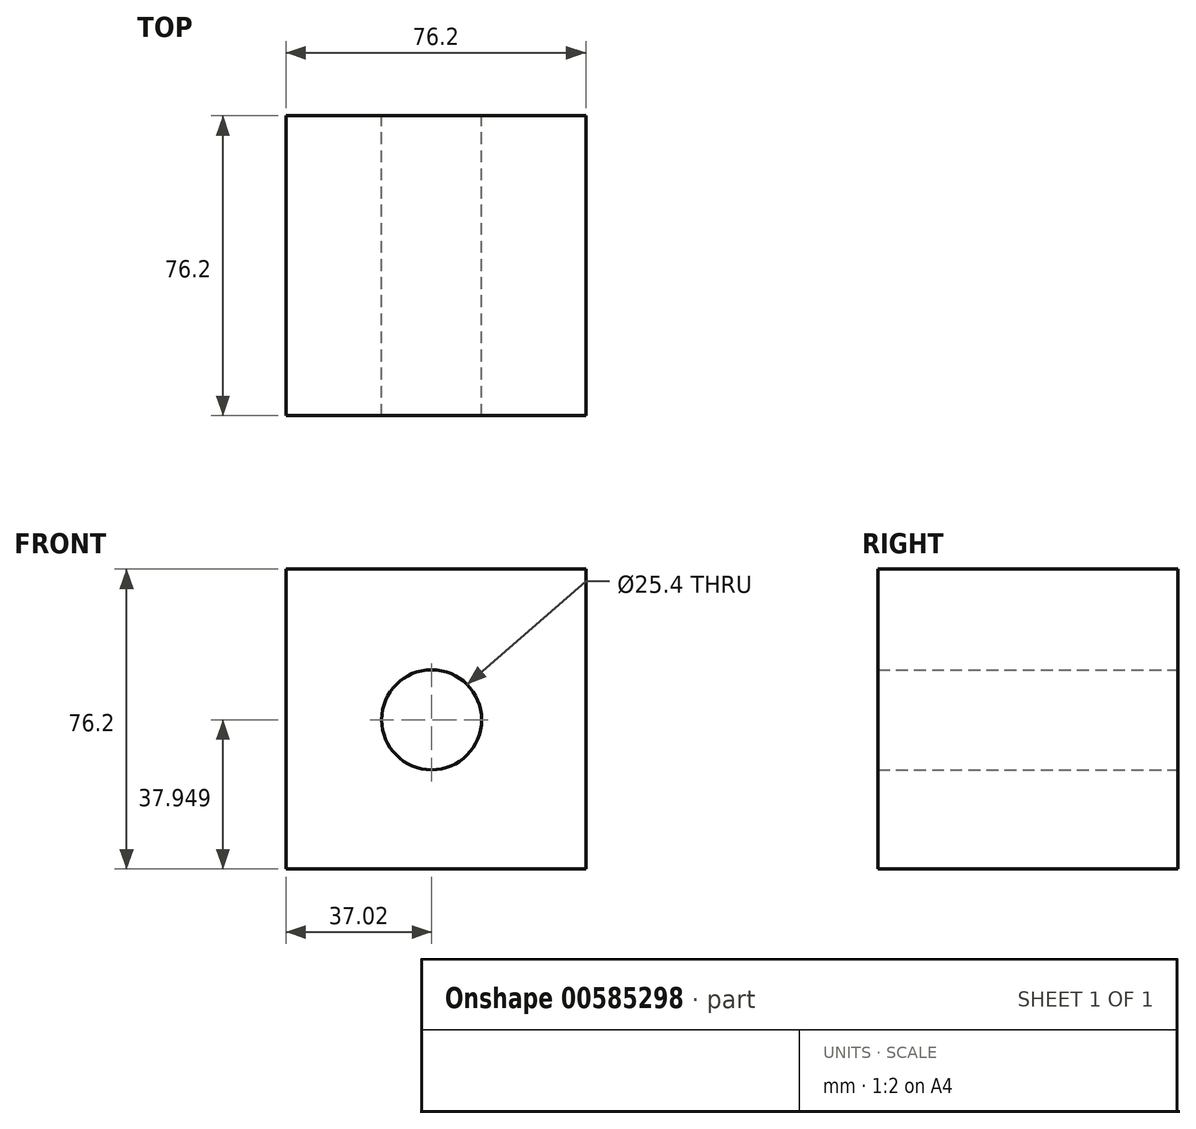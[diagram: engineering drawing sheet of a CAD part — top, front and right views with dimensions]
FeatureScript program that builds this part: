
annotation { "Feature Type Name" : "Feature", "Feature Type Description" : "" }
export const myFeature = defineFeature(function(context is Context, id is Id, definition is map)
    precondition{}
    {
        {
            var Q0;
            Q0=qCreatedBy(makeId("Front.planeOp"),FACE);
            var sketch = newSketch(context, id + "F0", { "sketchPlane" : qUnion([Q0])});
            skLineSegment(sketch, "E0.bottom", {"start": v(-37.02, 0) * mm, "end": v(39.18, 0) * mm});
            skLineSegment(sketch, "E0.top", {"start": v(-37.02, -76.2) * mm, "end": v(39.18, -76.2) * mm});
            skLineSegment(sketch, "E0.left", {"start": v(-37.02, 0) * mm, "end": v(-37.02, -76.2) * mm});
            skLineSegment(sketch, "E0.right", {"start": v(39.18, 0) * mm, "end": v(39.18, -76.2) * mm});
            skSolve(sketch);
        }
        {
            var Q0;
            Q0=makeQuery(id+"F0.imprint","IMPRINT",FACE,{"disambiguationData":[TD([[makeQuery(id+"F0.imprint","IMPRINT",EDGE,{"derivedFrom":sQuery(id+"F0.wireOp",EDGE,"E0.bottom")}),-1.0]])]});
            var sketch = newSketch(context, id + "F1", { "sketchPlane" : qUnion([Q0])});
            skSolve(sketch);
        }
        {
            var Q0;
            Q0=makeQuery(id+"F1.imprint","IMPRINT",FACE,{"disambiguationData":[TD([[makeQuery(id+"F1.imprint","IMPRINT",EDGE,{"derivedFrom":makeQuery(id+"F0.imprint","IMPRINT",EDGE,{"derivedFrom":sQuery(id+"F0.wireOp",EDGE,"E0.bottom")})}),-1.0]])]});
            var sketch = newSketch(context, id + "F2", { "sketchPlane" : qUnion([Q0])});
            skLineSegment(sketch, "E1", {"start": v(0, 0) * mm, "end": v(0, -38.1) * mm});
            skSolve(sketch);
        }
        {
            var Q0;
            Q0=makeQuery(id+"F1.imprint","IMPRINT",FACE,{"disambiguationData":[TD([[makeQuery(id+"F1.imprint","IMPRINT",EDGE,{"derivedFrom":makeQuery(id+"F0.imprint","IMPRINT",EDGE,{"derivedFrom":sQuery(id+"F0.wireOp",EDGE,"E0.bottom")})}),-1.0]])]});
            var sketch = newSketch(context, id + "F3", { "sketchPlane" : qUnion([Q0])});
            skPoint(sketch, "E2", {"position": v(0, -38.25) * mm});
            skSolve(sketch);
        }
        {
            var Q0;
            Q0=makeQuery(id+"F1.imprint","IMPRINT",FACE,{"disambiguationData":[TD([[makeQuery(id+"F1.imprint","IMPRINT",EDGE,{"derivedFrom":makeQuery(id+"F0.imprint","IMPRINT",EDGE,{"derivedFrom":sQuery(id+"F0.wireOp",EDGE,"E0.bottom")})}),-1.0]])]});
            extrude(context, id + "F4", {"entities" : qUnion([Q0]), "depth" : 76.2 * mm, "offsetDistance" : 25.4 * mm});
        }
        {
            var Q0;
            Q0=sQuery(id+"F3.wireOp",VERTEX,"E2");
            var Q1;
            Q1=makeQuery(id+"F4.opExtrude","SWEPT_BODY",BODY,{"disambiguationData":[OSD([sQuery(id+"F0.wireOp",EDGE,"E0.bottom"),sQuery(id+"F0.wireOp",EDGE,"E0.top"),sQuery(id+"F0.wireOp",EDGE,"E0.left"),sQuery(id+"F0.wireOp",EDGE,"E0.right")])]});
            hole(context, id + "F5", {"style" : HoleStyle.SIMPLE, "endStyle" : HoleEndStyle.THROUGH, "oppositeDirection" : true, "holeDiameter" : 25.4 * mm, "majorDiameter" : 6.35 * mm, "isTappedThrough" : true, "tappedDepth" : 12.7 * mm, "tapClearance" : 3, "locations" : qUnion([Q0]), "scope" : qUnion([Q1])});
        }
    });
